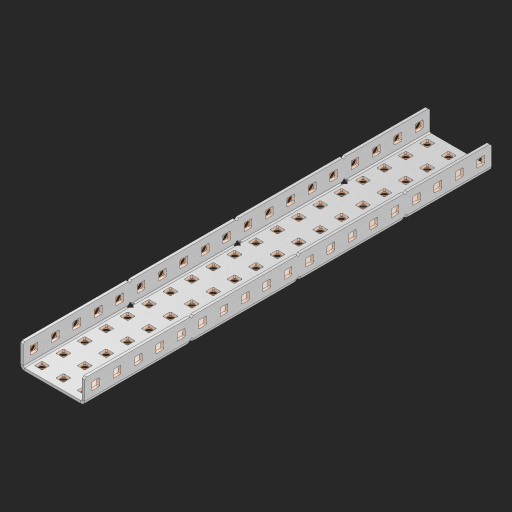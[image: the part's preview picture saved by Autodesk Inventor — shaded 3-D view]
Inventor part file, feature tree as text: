
AUTODESK INVENTOR PART (.ipt)
format: ipt  version: 2023 (Build 270158000, 158)  size: 1,320,960 bytes
history: native  units: in
note: dims shown in document units (in); Inventor stores cm internally (conversion verified against a paired STEP export)
features: other x100, extrude x94, sheet_metal_op x10, sketch x8, mirror x1, pattern_linear x1, chamfer x1
ambient origin geometry x8: Origin, YZ Plane, XZ Plane, XY Plane, X Axis, Y Axis, Z Axis, Center Point
bodies: Solid1 (feature_tree), Body (feature_tree)
feature tree (215):
  other  "Flange Pattern Plane"
  sheet_metal_op  "Flange Pattern"
  sheet_metal_op  "Body Pattern"
  other  "Arc Length"
  mirror  "Notch Mirror"
  pattern_linear  "Notch Pattern"  Spacing1=0.25in  [1 undecoded]
  chamfer  "End Chamfer"
  extrude  "Half Cut"  Depth=0.0625in
  sketch  "Sketch1"  dims[d0=1.5in]
  other  "Plate1"
  sketch  "Sketch2"  dims[d1=9.5in]
  other  "Plate2"
  sheet_metal_op  "Bend1"
  sheet_metal_op  "Corner1"
  sketch  "Sketch3"  dims[d2=0.0625in]
  other  "Flange Pattern Sketch"
  sketch  "Sketch7"  dims[d3=0.0625in]
  other  "Srf1"
  other  "Srf2"
  sketch  "Sketch8"  dims[d4=0.0312in]
  sketch  "Sketch9"  dims[d5=0.125in]
  other  "Srf91"
  sheet_metal_op  "Body Pattern Sketch"
  other  "Srf92"
  sketch  "Sketch13"  dims[d6=0.0625in]
  sketch  "Sketch14"  dims[d7=0.5in d8=90.0deg d9=0.0312in d10=0.25in d11=0.0625in d12=0.0625in d16=0.182in d17=0.02in d18=0.0625in d19=0.0in d20=0.25in d21=0.25in d46=0.172in d47=1.0in d48=0.0in d49=0.182in d50=0.02in d51=0.25in d52=0.25in d53=0.0625in d54=0.0in d55=0.172in d56=1.0in d57=0.0in d60=7.4803in d62=0.5in d63=1.1811in d65=0.5in d85=0.1473in d86=0.1782in d88=0.04in d89=0.0625in d90=0.0in d91=0.04in d92=0.0491in d95=2.5in d96=0.04in d97=0.25in d98=45.0deg d101=0.0in d102=2.497in d131=1.5in d132=7.4803in d134=0.5in d139=0.5in]
  other  "Srf856"
  other  "Srf1310"
  other  "Srf1311"
  other  "Srf1312"
  other  "Srf1376"
  other  "Srf1377"
  other  "Srf1728"
  other  "Srf1755"
  other  "Srf1878"
  other  "Srf1879"
  other  "Srf1880"
  other  "Srf1881"
  other  "Srf1882"
  other  "Srf1883"
  other  "Srf1884"
  other  "Srf1885"
  other  "Srf1886"
  other  "Srf1887"
  other  "Srf1888"
  other  "Srf1889"
  other  "Srf1890"
  other  "Srf1891"
  other  "Srf1892"
  other  "Srf1893"
  other  "Srf1894"
  other  "Srf1895"
  other  "Srf1896"
  other  "Srf1897"
  other  "Srf1898"
  other  "Srf1899"
  other  "Srf1900"
  other  "Srf1901"
  other  "Srf1902"
  other  "Srf1903"
  other  "Srf1904"
  other  "Srf1905"
  other  "Srf1906"
  other  "Srf1907"
  other  "Srf1908"
  other  "Srf1909"
  other  "Srf1942"
  other  "Srf1943"
  other  "Srf1944"
  other  "Srf1945"
  other  "Srf1946"
  other  "Srf1947"
  other  "Srf1948"
  other  "Srf1949"
  other  "Srf1950"
  other  "Srf1951"
  other  "Srf1952"
  other  "Srf1953"
  other  "Srf1954"
  other  "Srf1955"
  other  "Srf1956"
  other  "Srf1957"
  other  "Srf1958"
  other  "Srf1959"
  other  "Srf1960"
  other  "Srf1961"
  other  "Srf1962"
  other  "Srf1963"
  other  "Srf1964"
  other  "Srf1965"
  other  "Srf1966"
  other  "Srf1967"
  other  "Srf1968"
  other  "Srf1969"
  other  "Srf1970"
  other  "Srf1971"
  other  "Srf1972"
  other  "Srf1973"
  other  "Srf1974"
  other  "Srf1975"
  other  "Srf1976"
  other  "Srf1977"
  other  "Srf1978"
  other  "Srf1979"
  other  "Srf1980"
  other  "Srf1981"
  other  "Srf1982"
  other  "Srf1983"
  other  "Srf1984"
  other  "Srf1985"
  other  "Srf1986"
  other  "Srf1987"
  other  "Srf1988"
  other  "Srf1989"
  other  "Srf1990"
  other  "Srf1991"
  other  "Srf1992"
  sheet_metal_op  "Flange Stamp"
  sheet_metal_op  "Flange Circle"
  sheet_metal_op  "Body Stamp"
  sheet_metal_op  "Body Circle"
  sheet_metal_op  "Notch"
  extrude  "ExtrusionSrf2"  Depth=0.0625in
  extrude  "ExtrusionSrf92"  Depth=1.5in
  extrude  "ExtrusionSrf856"  Depth=0.02in
  extrude  "ExtrusionSrf1310"  Depth=0.0625in
  extrude  "ExtrusionSrf1311"  TaperAngle=0.0deg  [1 undecoded]
  extrude  "ExtrusionSrf1312"  Depth=0.25in
  extrude  "ExtrusionSrf1376"  Depth=0.25in
  extrude  "ExtrusionSrf1377"  Depth=1.5in
  extrude  "ExtrusionSrf1728"  Depth=1.5in TaperAngle=0.0deg
  extrude  "ExtrusionSrf1755"  Depth=1.5in
  extrude  "ExtrusionSrf1878"  Depth=0.02in
  extrude  "ExtrusionSrf1879"  Depth=0.25in
  extrude  "ExtrusionSrf1880"  Depth=0.25in
  extrude  "ExtrusionSrf1881"  Depth=0.0625in
  extrude  "ExtrusionSrf1882"  TaperAngle=0.0deg  [1 undecoded]
  extrude  "ExtrusionSrf1883"  Depth=1.5in
  extrude  "ExtrusionSrf1884"  Depth=1.5in TaperAngle=0.0deg
  extrude  "ExtrusionSrf1885"  Depth=1.5in
  extrude  "ExtrusionSrf1886"  Depth=1.5in
  extrude  "ExtrusionSrf1887"  Depth=1.5in
  extrude  "ExtrusionSrf1888"  Depth=1.5in
  extrude  "ExtrusionSrf1889"  Depth=1.5in
  extrude  "ExtrusionSrf1890"  Depth=0.0625in
  extrude  "ExtrusionSrf1891"  TaperAngle=0.0deg  [1 undecoded]
  extrude  "ExtrusionSrf1892"  Depth=1.5in
  extrude  "ExtrusionSrf1893"  Depth=1.5in
  extrude  "ExtrusionSrf1894"  Depth=1.5in
  extrude  "ExtrusionSrf1895"  Depth=0.25in TaperAngle=45.0deg
  extrude  "ExtrusionSrf1896"  TaperAngle=0.0deg  [1 undecoded]
  extrude  "ExtrusionSrf1897"  Depth=1.5in
  extrude  "ExtrusionSrf1898"  Depth=1.5in
  extrude  "ExtrusionSrf1899"  Depth=1.5in
  extrude  "ExtrusionSrf1900"  Depth=1.5in
  extrude  "ExtrusionSrf1901"  Depth=1.5in
  extrude  "ExtrusionSrf1902"  [1 undecoded]
  extrude  "ExtrusionSrf1903"  [1 undecoded]
  extrude  "ExtrusionSrf1904"  [1 undecoded]
  extrude  "ExtrusionSrf1905"  [1 undecoded]
  extrude  "ExtrusionSrf1906"  [1 undecoded]
  extrude  "ExtrusionSrf1907"  [1 undecoded]
  extrude  "ExtrusionSrf1908"  [1 undecoded]
  extrude  "ExtrusionSrf1909"  [1 undecoded]
  extrude  "ExtrusionSrf1942"  [1 undecoded]
  extrude  "ExtrusionSrf1943"  [1 undecoded]
  extrude  "ExtrusionSrf1944"  [1 undecoded]
  extrude  "ExtrusionSrf1945"  [1 undecoded]
  extrude  "ExtrusionSrf1946"  [1 undecoded]
  extrude  "ExtrusionSrf1947"  [1 undecoded]
  extrude  "ExtrusionSrf1948"  [1 undecoded]
  extrude  "ExtrusionSrf1949"  [1 undecoded]
  extrude  "ExtrusionSrf1950"  [1 undecoded]
  extrude  "ExtrusionSrf1951"  [1 undecoded]
  extrude  "ExtrusionSrf1952"  [1 undecoded]
  extrude  "ExtrusionSrf1953"  [1 undecoded]
  extrude  "ExtrusionSrf1954"  [1 undecoded]
  extrude  "ExtrusionSrf1955"  [1 undecoded]
  extrude  "ExtrusionSrf1956"  [1 undecoded]
  extrude  "ExtrusionSrf1957"  [1 undecoded]
  extrude  "ExtrusionSrf1958"  [1 undecoded]
  extrude  "ExtrusionSrf1959"  [1 undecoded]
  extrude  "ExtrusionSrf1960"  [1 undecoded]
  extrude  "ExtrusionSrf1961"  [1 undecoded]
  extrude  "ExtrusionSrf1962"  [1 undecoded]
  extrude  "ExtrusionSrf1963"  [1 undecoded]
  extrude  "ExtrusionSrf1964"  [1 undecoded]
  extrude  "ExtrusionSrf1965"  [1 undecoded]
  extrude  "ExtrusionSrf1966"  [1 undecoded]
  extrude  "ExtrusionSrf1967"  [1 undecoded]
  extrude  "ExtrusionSrf1968"  [1 undecoded]
  extrude  "ExtrusionSrf1969"  [1 undecoded]
  extrude  "ExtrusionSrf1970"  [1 undecoded]
  extrude  "ExtrusionSrf1971"  [1 undecoded]
  extrude  "ExtrusionSrf1972"  [1 undecoded]
  extrude  "ExtrusionSrf1973"  [1 undecoded]
  extrude  "ExtrusionSrf1974"  [1 undecoded]
  extrude  "ExtrusionSrf1975"  [1 undecoded]
  extrude  "ExtrusionSrf1976"  [1 undecoded]
  extrude  "ExtrusionSrf1977"  [1 undecoded]
  extrude  "ExtrusionSrf1978"  [1 undecoded]
  extrude  "ExtrusionSrf1979"  [1 undecoded]
  extrude  "ExtrusionSrf1980"  [1 undecoded]
  extrude  "ExtrusionSrf1981"  [1 undecoded]
  extrude  "ExtrusionSrf1982"  [1 undecoded]
  extrude  "ExtrusionSrf1983"  [1 undecoded]
  extrude  "ExtrusionSrf1984"  [1 undecoded]
  extrude  "ExtrusionSrf1985"  [1 undecoded]
  extrude  "ExtrusionSrf1986"  [1 undecoded]
  extrude  "ExtrusionSrf1987"  [1 undecoded]
  extrude  "ExtrusionSrf1988"  [1 undecoded]
  extrude  "ExtrusionSrf1989"  [1 undecoded]
  extrude  "ExtrusionSrf1990"  [1 undecoded]
  extrude  "ExtrusionSrf1991"  [1 undecoded]
  extrude  "ExtrusionSrf1992"  [1 undecoded]
note: 64 required parameter values undecoded (feature->parameter linkage not recoverable at this tier; creation-order binding heuristic only, values carry confidence <= 0.55)
